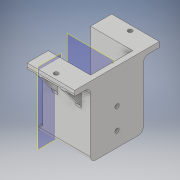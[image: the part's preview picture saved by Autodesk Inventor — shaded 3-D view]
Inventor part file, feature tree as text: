
AUTODESK INVENTOR PART (.ipt)
format: ipt  version: 2019.4 (Build 234330000, 330)  size: 220,160 bytes
history: native  units: mm
features: extrude x6, fillet x6, sketch x6, plane x2, pattern_linear x1, mirror x1
ambient origin geometry x8: Origin, YZ Plane, XZ Plane, XY Plane, X Axis, Y Axis, Z Axis, Center Point
bodies: Solid1 (feature_tree)
feature tree (22):
  extrude  "Extrusion1"  Depth=40.0mm
  extrude  "Extrusion2"  Depth=67.0mm TaperAngle=0.0deg
  plane  "Work Plane1"
  extrude  "Extrusion3"  Depth=50.0mm
  plane  "Work Plane2"
  extrude  "Extrusion4"  Depth=20.0mm
  pattern_linear  "Rectangular Pattern1"  Spacing1=15.0mm  [1 undecoded]
  fillet  "Fillet1"  [1 undecoded]
  fillet  "Fillet2"  Radius=25.0mm
  mirror  "Mirror1"
  fillet  "Fillet3"  Radius=15.0mm
  fillet  "Fillet4"  Radius=5.0mm
  fillet  "Fillet5"  Radius=20.0mm
  fillet  "Fillet6"  Radius=5.0mm
  extrude  "Extrusion6"  Depth=5.0mm
  extrude  "Extrusion7"  Depth=5.0mm
  sketch  "Sketch1"  dims[d0=40.0mm d1=40.0mm]
  sketch  "Sketch2"  dims[d2=5.0mm d3=67.0mm d4=0.0mm]
  sketch  "Sketch3"  dims[d5=50.0mm d6=50.0mm]
  sketch  "Sketch4"  dims[d7=5.0mm d8=0.0mm d9=20.0mm]
  sketch  "Sketch6"  dims[d10=45.0mm]
  sketch  "Sketch7"  dims[d11=5.0mm d12=15.0mm d13=0.0mm d14=-11.25mm d15=25.0mm d17=15.0mm d18=5.0mm d19=0.0mm d20=20.0mm d22=22.5mm d23=5.0mm d24=5.0mm d25=5.0mm d26=5.0mm d27=5.0mm d28=5.0mm d35=5.0mm d36=5.0mm d37=4.0mm d38=4.0mm d39=5.0mm d40=0.0mm d41=14.0mm d42=20.0mm d43=180.0deg d44=4.0mm d45=4.0mm d46=5.0mm d47=0.0mm]
note: 2 required parameter values undecoded (feature->parameter linkage not recoverable at this tier; creation-order binding heuristic only, values carry confidence <= 0.55)
